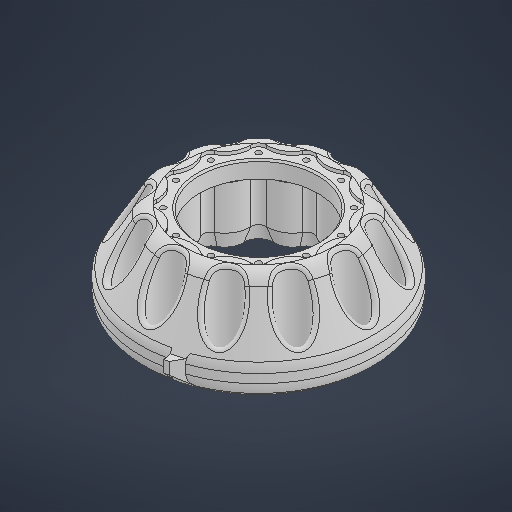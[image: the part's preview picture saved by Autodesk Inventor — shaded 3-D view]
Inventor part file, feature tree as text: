
AUTODESK INVENTOR PART (.ipt)
format: ipt  version: 2025.1 (Build 291241000, 241)  size: 2,225,152 bytes
history: native  units: mm
features: chamfer x6, fillet x4, sketch x3, extrude x3, plane x2, pattern_circular x2, revolve x1, projected_geometry x1
ambient origin geometry x8: Origin, YZ Plane, XZ Plane, XY Plane, X Axis, Y Axis, Z Axis, Center Point
bodies: Solid1 (feature_tree)
feature tree (22):
  sketch  "Sketch1"  dims[d0=42.0mm d1=42.0mm]
  extrude  "Extrusion1"  Depth=42.0mm
  extrude  "Extrusion2"  Depth=55.0mm
  plane  "Work Plane2"
  fillet  "Fillet8"  Radius=17.2mm
  pattern_circular  "Circular Pattern1"  Count=5  [1 undecoded]
  extrude  "Extrusion9"  Depth=10.0mm TaperAngle=360.0deg
  pattern_circular  "Circular Pattern3"  Count=7  [1 undecoded]
  chamfer  "Chamfer1"  Angle=15.0deg  [1 undecoded]
  chamfer  "Chamfer6"  Angle=15.0deg  [1 undecoded]
  chamfer  "Chamfer7"  Distance=40.0mm
  chamfer  "Chamfer8"  Distance=3.2mm
  sketch  "Sketch12"  dims[d6=2.0mm d7=0.0mm d8=50.0mm d9=0.0mm d13=120.0mm d14=360.0deg d16=70.0mm d37=15.0deg d38=15.0deg d42=40.0mm d43=3.2mm d44=40.0mm d45=5.5mm d47=10.0mm d48=0.0mm d51=4.5mm d52=5.0mm d53=2.0mm d54=45.0deg d70=120.0mm d71=360.0deg d73=4.0mm d74=10.0mm d75=45.0deg d76=4.0mm d77=30.0mm d78=45.0deg d79=1.0mm d80=30.0mm d81=45.0deg d83=-40.0mm d84=12.0mm d85=45.0deg d86=5.0mm d87=0.349066mm d88=5.0mm d89=2.0mm d90=45.0deg d91=20.0mm d92=35.0mm d93=45.0deg d94=2.0mm d96=2.268928mm d97=90.0deg d98=10.0mm d99=10.0mm d100=1.5mm]
  plane  "Work Plane3"
  revolve  "Revolution1"  [1 undecoded]
  chamfer  "Chamfer9"  Distance=5.5mm
  chamfer  "Chamfer10"  Distance=10.0mm
  fillet  "Fillet6"  Radius=4.5mm
  fillet  "Fillet4"  Radius=5.0mm
  fillet  "Fillet7"  Radius=120.0mm
  sketch  "Sketch11"  dims[d2=140.0mm d3=55.0mm d5=17.2mm]
  projected_geometry  "Projected Loop8"
note: 5 required parameter values undecoded (feature->parameter linkage not recoverable at this tier; creation-order binding heuristic only, values carry confidence <= 0.55)